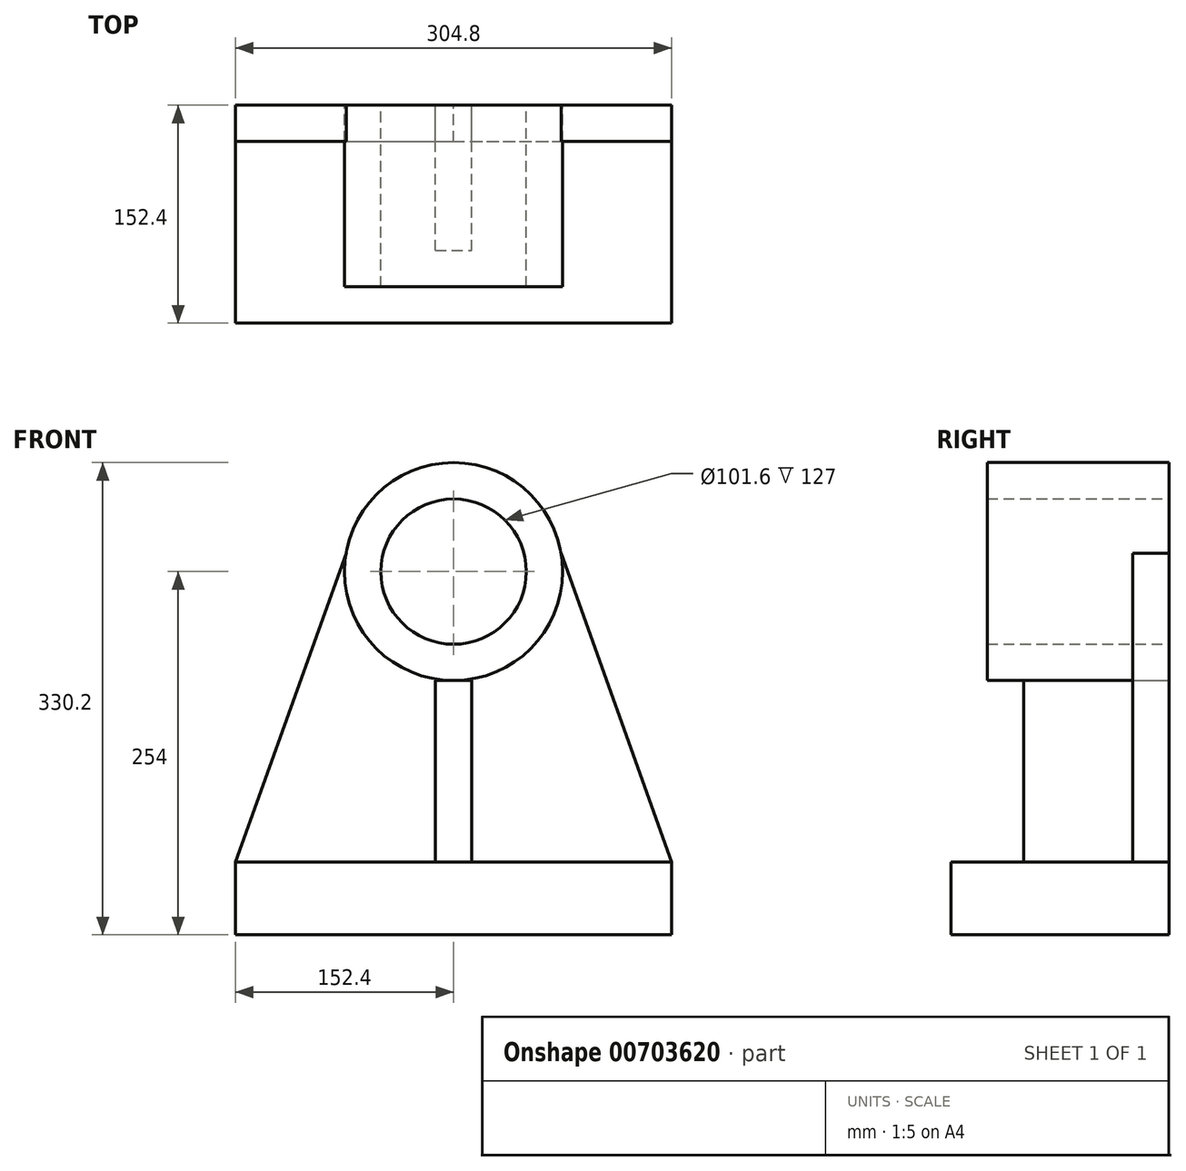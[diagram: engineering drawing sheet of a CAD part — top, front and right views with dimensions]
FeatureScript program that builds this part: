
annotation { "Feature Type Name" : "Feature", "Feature Type Description" : "" }
export const myFeature = defineFeature(function(context is Context, id is Id, definition is map)
    precondition{}
    {
        {
            var Q0;
            Q0=qCreatedBy(makeId("Front.planeOp"),FACE);
            var sketch = newSketch(context, id + "F0", { "sketchPlane" : qUnion([Q0])});
            skLineSegment(sketch, "E0.bottom", {"start": v(-152.4, 25.4) * mm, "end": v(152.4, 25.4) * mm});
            skLineSegment(sketch, "E0.top", {"start": v(-152.4, -25.4) * mm, "end": v(152.4, -25.4) * mm});
            skLineSegment(sketch, "E0.left", {"start": v(-152.4, 25.4) * mm, "end": v(-152.4, -25.4) * mm});
            skLineSegment(sketch, "E0.right", {"start": v(152.4, 25.4) * mm, "end": v(152.4, -25.4) * mm});
            skPoint(sketch, "E0.middle", {"position": v(0, 0) * mm});
            skLineSegment(sketch, "E1", {"start": v(-12.7, 25.4) * mm, "end": v(-12.7, 152.4) * mm});
            skLineSegment(sketch, "E2", {"start": v(-12.7, 152.4) * mm, "end": v(12.7, 152.4) * mm});
            skLineSegment(sketch, "E3", {"start": v(12.7, 152.4) * mm, "end": v(12.7, 25.4) * mm});
            skCircle(sketch, "E4", {"center": v(0, 228.6) * mm, "radius": 76.2 * mm});
            skCircle(sketch, "E5", {"center": v(0, 228.6) * mm, "radius": 50.8 * mm});
            skLineSegment(sketch, "E6", {"start": v(-75.13, 241.3) * mm, "end": v(-152.4, 25.4) * mm});
            skLineSegment(sketch, "E7", {"start": v(75.13, 241.3) * mm, "end": v(152.4, 25.4) * mm});
            skSolve(sketch);
        }
        {
            var Q0;
            Q0=makeQuery(id+"F0.imprint","IMPRINT",FACE,{"disambiguationData":[TD([[makeQuery(id+"F0.imprint","IMPRINT",EDGE,{"derivedFrom":sQuery(id+"F0.wireOp",EDGE,"E0.top")}),1.0]])]});
            extrude(context, id + "F1", {"entities" : qUnion([Q0]), "depth" : 152.4 * mm, "offsetDistance" : 25.4 * mm});
        }
        {
            var Q0;
            Q0=makeQuery(id+"F0.imprint","IMPRINT",FACE,{"disambiguationData":[TD([[makeQuery(id+"F0.imprint","IMPRINT",EDGE,{"derivedFrom":sQuery(id+"F0.wireOp",EDGE,"E5")}),-1.0]])]});
            extrude(context, id + "F2", {"entities" : qUnion([Q0]), "depth" : 127 * mm, "offsetDistance" : 25.4 * mm});
        }
        {
            var Q0;
            {var subQ0=sQuery(id+"F0.wireOp",EDGE,"E3");Q0=makeQuery(id+"F0.imprint","IMPRINT",FACE,{"disambiguationData":[TD([[makeQuery(id+"F0.imprint","IMPRINT",EDGE,{"derivedFrom":subQ0}),1.0]])]});}
            var Q1;
            {var subQ1=sQuery(id+"F0.wireOp",EDGE,"E1");Q1=makeQuery(id+"F0.imprint","IMPRINT",FACE,{"disambiguationData":[TD([[makeQuery(id+"F0.imprint","IMPRINT",EDGE,{"derivedFrom":subQ1}),1.0]])]});}
            extrude(context, id + "F3", {"entities" : qUnion([Q0, Q1]), "depth" : 25.4 * mm, "offsetDistance" : 25.4 * mm});
        }
        {
            var Q0;
            {var subQ3=sQuery(id+"F0.wireOp",EDGE,"E1");Q0=makeQuery(id+"F0.imprint","IMPRINT",FACE,{"disambiguationData":[TD([[makeQuery(id+"F0.imprint","IMPRINT",EDGE,{"derivedFrom":subQ3}),-1.0]])]});}
            extrude(context, id + "F4", {"entities" : qUnion([Q0]), "depth" : 101.6 * mm, "offsetDistance" : 25.4 * mm});
        }
    });
